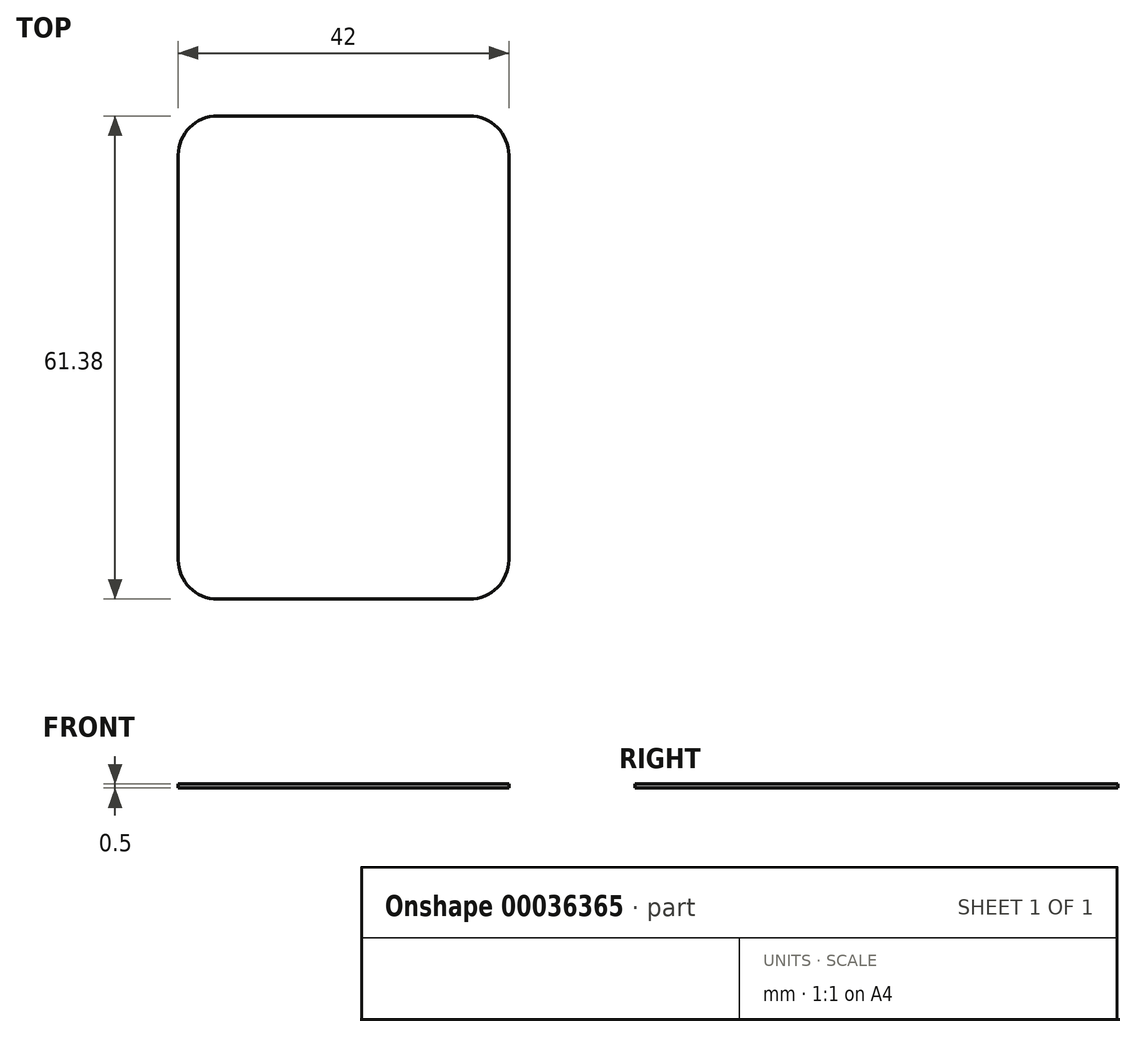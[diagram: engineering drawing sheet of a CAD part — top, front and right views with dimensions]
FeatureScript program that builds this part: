
annotation { "Feature Type Name" : "Feature", "Feature Type Description" : "" }
export const myFeature = defineFeature(function(context is Context, id is Id, definition is map)
    precondition{}
    {
        {
            var Q0;
            Q0=qCreatedBy(makeId("Top.planeOp"),FACE);
            var sketch = newSketch(context, id + "F0", { "sketchPlane" : qUnion([Q0])});
            skLineSegment(sketch, "E0.bottom", {"start": v(-5, 0) * mm, "end": v(-37, 0) * mm});
            skLineSegment(sketch, "E0.top", {"start": v(-5, -61.38) * mm, "end": v(-37, -61.38) * mm});
            skLineSegment(sketch, "E0.left", {"start": v(0, -5) * mm, "end": v(0, -56.38) * mm});
            skLineSegment(sketch, "E0.right", {"start": v(-42, -5) * mm, "end": v(-42, -56.38) * mm});
            skPoint(sketch, "E1.visualSharp", {"position": v(-42, 0) * mm});
            skArc(sketch, "E1.filletArc", {"start": v(-37, 0) * mm, "mid": v(-40.54, -1.46) * mm, "end": v(-42, -5) * mm});
            skPoint(sketch, "E2.visualSharp", {"position": v(0, 0) * mm});
            skArc(sketch, "E2.filletArc", {"start": v(0, -5) * mm, "mid": v(-1.46, -1.46) * mm, "end": v(-5, 0) * mm});
            skPoint(sketch, "E3.visualSharp", {"position": v(0, -61.38) * mm});
            skArc(sketch, "E3.filletArc", {"start": v(-5, -61.38) * mm, "mid": v(-1.46, -59.92) * mm, "end": v(0, -56.38) * mm});
            skPoint(sketch, "E4.visualSharp", {"position": v(-42, -61.38) * mm});
            skArc(sketch, "E4.filletArc", {"start": v(-42, -56.38) * mm, "mid": v(-40.54, -59.92) * mm, "end": v(-37, -61.38) * mm});
            skSolve(sketch);
        }
        {
            var Q0;
            Q0=makeQuery(id+"F0.imprint","IMPRINT",FACE,{"disambiguationData":[TD([[makeQuery(id+"F0.imprint","IMPRINT",EDGE,{"derivedFrom":sQuery(id+"F0.wireOp",EDGE,"E0.bottom")}),1.0]])]});
            extrude(context, id + "F1", {"entities" : qUnion([Q0]), "depth" : .5 * mm, "offsetDistance" : 25 * mm});
        }
    });
